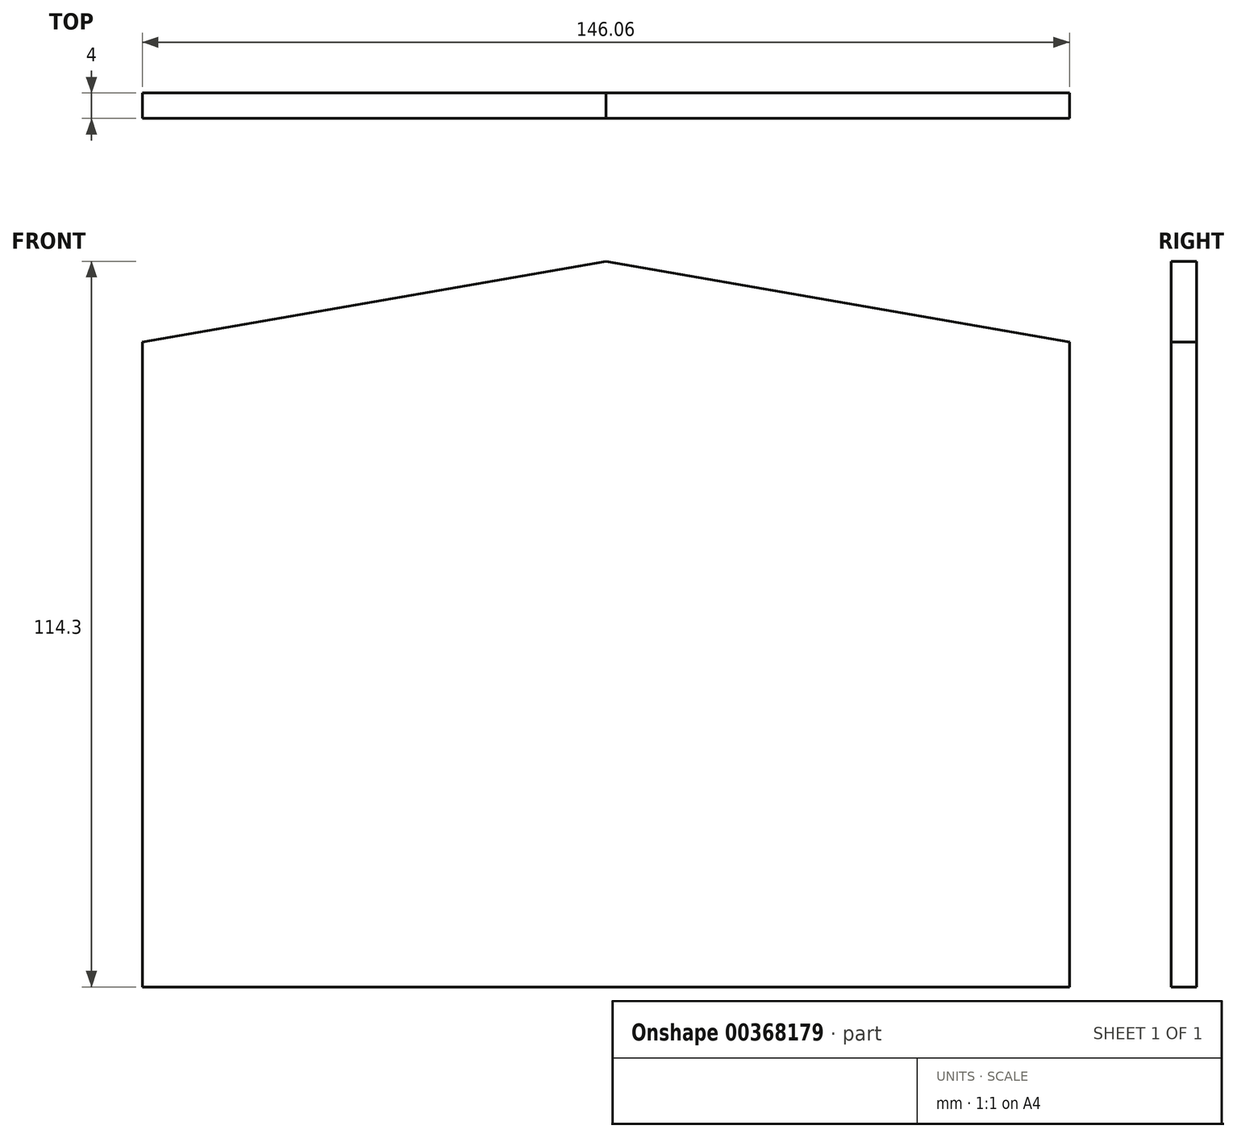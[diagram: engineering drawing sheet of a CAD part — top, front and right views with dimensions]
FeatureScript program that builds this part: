
annotation { "Feature Type Name" : "Feature", "Feature Type Description" : "" }
export const myFeature = defineFeature(function(context is Context, id is Id, definition is map)
    precondition{}
    {
        {
            var Q0;
            Q0=qCreatedBy(makeId("Front.planeOp"),FACE);
            var sketch = newSketch(context, id + "F0", { "sketchPlane" : qUnion([Q0])});
            skLineSegment(sketch, "E0.top", {"start": v(73.02, -50.8) * mm, "end": v(-73.03, -50.8) * mm});
            skLineSegment(sketch, "E0.left", {"start": v(73.03, 50.8) * mm, "end": v(73.02, -50.8) * mm});
            skLineSegment(sketch, "E0.right", {"start": v(-73.02, 50.8) * mm, "end": v(-73.03, -50.8) * mm});
            skPoint(sketch, "E0.middle", {"position": v(0, 0) * mm});
            skLineSegment(sketch, "E1", {"start": v(-73.03, 50.8) * mm, "end": v(0, 63.5) * mm});
            skLineSegment(sketch, "E2", {"start": v(0, 63.5) * mm, "end": v(73.03, 50.8) * mm});
            skLineSegment(sketch, "E3", {"start": v(-73.03, 50.8) * mm, "end": v(73.03, 50.8) * mm, "construction": true});
            skSolve(sketch);
        }
        {
            var Q0;
            Q0=makeQuery(id+"F0.imprint","IMPRINT",FACE,{"disambiguationData":[TD([[makeQuery(id+"F0.imprint","IMPRINT",EDGE,{"derivedFrom":sQuery(id+"F0.wireOp",EDGE,"E0.top")}),-1.0]])]});
            extrude(context, id + "F1", {"entities" : qUnion([Q0]), "depth" : 4 * mm});
        }
    });
